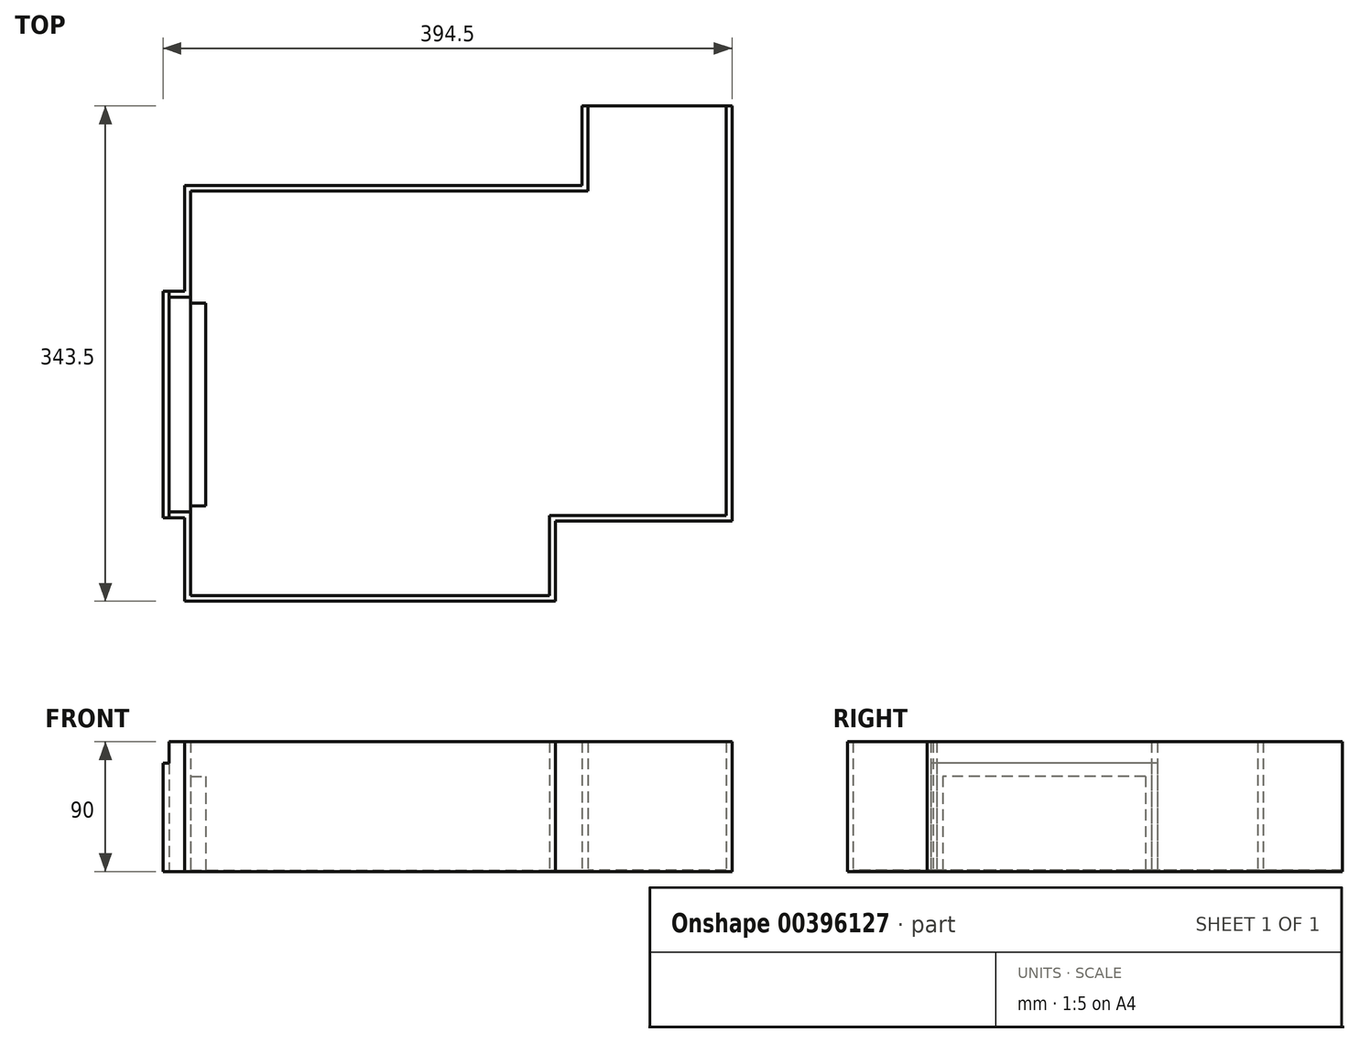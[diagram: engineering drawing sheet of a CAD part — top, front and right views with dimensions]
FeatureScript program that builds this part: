
annotation { "Feature Type Name" : "Feature", "Feature Type Description" : "" }
export const myFeature = defineFeature(function(context is Context, id is Id, definition is map)
    precondition{}
    {
        {
            var Q0;
            Q0=qCreatedBy(makeId("Top.planeOp"),FACE);
            var sketch = newSketch(context, id + "F0", { "sketchPlane" : qUnion([Q0])});
            skLineSegment(sketch, "E0.bottom", {"start": v(0, 0) * mm, "end": v(275.5, 0) * mm});
            skLineSegment(sketch, "E0.top", {"start": v(0, -280.5) * mm, "end": v(249, -280.5) * mm});
            skLineSegment(sketch, "E0.left", {"start": v(0, 0) * mm, "end": v(0, -280.5) * mm});
            skLineSegment(sketch, "E0.right", {"start": v(371.5, 0) * mm, "end": v(371.5, -225) * mm});
            skLineSegment(sketch, "E1.top", {"start": v(249, -225) * mm, "end": v(371.5, -225) * mm});
            skLineSegment(sketch, "E1.left", {"start": v(249, -280.5) * mm, "end": v(249, -225) * mm});
            skLineSegment(sketch, "E2.top", {"start": v(371.5, 59) * mm, "end": v(275.5, 59) * mm});
            skLineSegment(sketch, "E2.left", {"start": v(371.5, 0) * mm, "end": v(371.5, 59) * mm});
            skLineSegment(sketch, "E2.right", {"start": v(275.5, 0) * mm, "end": v(275.5, 59) * mm});
            skLineSegment(sketch, "E3.bottom", {"start": v(0, -77.75) * mm, "end": v(10.5, -77.75) * mm});
            skLineSegment(sketch, "E3.top", {"start": v(0, -218.25) * mm, "end": v(10.5, -218.25) * mm});
            skLineSegment(sketch, "E3.left", {"start": v(0, -77.75) * mm, "end": v(0, -218.25) * mm});
            skLineSegment(sketch, "E3.right", {"start": v(10.5, -77.75) * mm, "end": v(10.5, -218.25) * mm});
            skLineSegment(sketch, "E4.bottom", {"start": v(0, -73.5) * mm, "end": v(-15, -73.5) * mm});
            skLineSegment(sketch, "E4.top", {"start": v(0, -222.5) * mm, "end": v(-15, -222.5) * mm});
            skLineSegment(sketch, "E4.left", {"start": v(0, -73.5) * mm, "end": v(0, -222.5) * mm});
            skLineSegment(sketch, "E4.right", {"start": v(-15, -73.5) * mm, "end": v(-15, -222.5) * mm});
            skPoint(sketch, "E5", {"position": v(-15, -148) * mm});
            skPoint(sketch, "E6", {"position": v(10.5, -148) * mm});
            skLineSegment(sketch, "E7", {"start": v(-19, -69.5) * mm, "end": v(-19, -226.5) * mm});
            skLineSegment(sketch, "E8", {"start": v(-19, -226.5) * mm, "end": v(-4, -226.5) * mm});
            skLineSegment(sketch, "E9", {"start": v(-4, -226.5) * mm, "end": v(-4, -284.5) * mm});
            skLineSegment(sketch, "E10", {"start": v(-4, -284.5) * mm, "end": v(253, -284.5) * mm});
            skLineSegment(sketch, "E11", {"start": v(253, -284.5) * mm, "end": v(253, -229) * mm});
            skLineSegment(sketch, "E12", {"start": v(253, -229) * mm, "end": v(375.5, -229) * mm});
            skLineSegment(sketch, "E13", {"start": v(375.5, -229) * mm, "end": v(375.5, 59) * mm});
            skLineSegment(sketch, "E14", {"start": v(375.5, 59) * mm, "end": v(371.5, 59) * mm});
            skLineSegment(sketch, "E15", {"start": v(275.5, 59) * mm, "end": v(271.5, 59) * mm});
            skLineSegment(sketch, "E16", {"start": v(271.5, 59) * mm, "end": v(271.5, 4) * mm});
            skLineSegment(sketch, "E17", {"start": v(271.5, 4) * mm, "end": v(-4, 4) * mm});
            skLineSegment(sketch, "E18", {"start": v(-4, 4) * mm, "end": v(-4, -69.5) * mm});
            skLineSegment(sketch, "E19", {"start": v(-4, -69.5) * mm, "end": v(-19, -69.5) * mm});
            skSolve(sketch);
        }
        {
            var Q0;
            {var subQ3=sQuery(id+"F0.wireOp",EDGE,"E0.bottom");Q0=makeQuery(id+"F0.imprint","IMPRINT",FACE,{"disambiguationData":[TD([[makeQuery(id+"F0.imprint","IMPRINT",EDGE,{"derivedFrom":subQ3}),1.0]])]});}
            extrude(context, id + "F1", {"entities" : qUnion([Q0]), "depth" : 90 * mm});
        }
        {
            var Q0;
            {var subQ5=sQuery(id+"F0.wireOp",EDGE,"E0.bottom");Q0=makeQuery(id+"F0.imprint","IMPRINT",FACE,{"disambiguationData":[TD([[makeQuery(id+"F0.imprint","IMPRINT",EDGE,{"derivedFrom":subQ5}),-1.0]])]});}
            extrude(context, id + "F2", {"entities" : qUnion([Q0]), "operationType" : NewBodyOperationType.ADD, "depth" : 1 * mm});
        }
        {
            var Q0;
            {var subQ0=sQuery(id+"F0.wireOp",EDGE,"E3.bottom");Q0=makeQuery(id+"F0.imprint","IMPRINT",FACE,{"disambiguationData":[TD([[makeQuery(id+"F0.imprint","IMPRINT",EDGE,{"derivedFrom":subQ0}),-1.0]])]});}
            extrude(context, id + "F3", {"entities" : qUnion([Q0]), "operationType" : NewBodyOperationType.ADD, "depth" : 66 * mm});
        }
        {
            var Q0;
            Q0=makeQuery(id+"F1.opExtrude","SWEPT_FACE",FACE,{"disambiguationData":[OSD([sQuery(id+"F0.wireOp",EDGE,"E7")])]});
            var sketch = newSketch(context, id + "F4", { "sketchPlane" : qUnion([Q0])});
            skLineSegment(sketch, "E20.bottom", {"start": v(69.5, 75.13) * mm, "end": v(226.5, 75.13) * mm});
            skLineSegment(sketch, "E20.top", {"start": v(69.5, 165.13) * mm, "end": v(226.5, 165.13) * mm});
            skLineSegment(sketch, "E20.left", {"start": v(69.5, 75.13) * mm, "end": v(69.5, 165.13) * mm});
            skLineSegment(sketch, "E20.right", {"start": v(226.5, 75.13) * mm, "end": v(226.5, 165.13) * mm});
            skSolve(sketch);
        }
        {
            var Q0;
            Q0=makeQuery(id+"F4.imprint","IMPRINT",FACE,{"disambiguationData":[TD([[makeQuery(id+"F4.imprint","IMPRINT",EDGE,{"derivedFrom":sQuery(id+"F4.wireOp",EDGE,"E20.bottom")}),1.0]])]});
            extrude(context, id + "F5", {"entities" : qUnion([Q0]), "operationType" : NewBodyOperationType.REMOVE, "oppositeDirection" : true, "depth" : 4 * mm});
        }
    });
